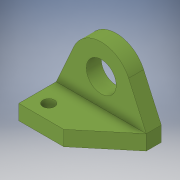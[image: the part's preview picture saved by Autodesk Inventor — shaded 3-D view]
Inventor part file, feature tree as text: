
AUTODESK INVENTOR PART (.ipt)
format: ipt  version: 2018 (Build 220112000, 112)  size: 145,920 bytes
history: native  units: in
note: dims shown in document units (in); Inventor stores cm internally (conversion verified against a paired STEP export)
features: extrude x4, sketch x4, projected_geometry x3, other x3, reference x1
ambient origin geometry x8: Origin, YZ Plane, XZ Plane, XY Plane, X Axis, Y Axis, Z Axis, Center Point
bodies: Solid1 (feature_tree)
feature tree (15):
  extrude  "Extrusion1"  Depth=0.195in
  extrude  "Extrusion2"  Depth=0.25in
  extrude  "Extrusion3"  Depth=0.25in
  extrude  "Extrusion4"  Depth=0.25in TaperAngle=0.0deg
  sketch  "Sketch1"  dims[d0=0.195in d1=0.195in]
  sketch  "Sketch2"  dims[d2=1.0in d3=0.25in]
  projected_geometry  "Projected Loop1"
  reference  "Reference1"
  sketch  "Sketch3"  dims[d4=0.125in d5=0.25in]
  projected_geometry  "Projected Loop2"
  sketch  "Sketch4"  dims[d6=0.75in d7=0.25in d8=0.0in d9=0.25in d10=0.5in d11=0.25in d12=0.0in d13=0.125in d14=0.0in d15=1.0in d16=0.0in]
  projected_geometry  "Projected Loop3"
  parser-record x1  (decoder bookkeeping rows leaked as tree rows — omitted from the tree; the rows remain in map.json)
  other  "Assembly2.iam"
  other  "0_375_Hex_ID_x_1_125_OD_x_0_313_WD_Flanged_Bearing_217-2735:2"
note: 1 file-system path scrubbed to <path> (originals preserved in map.json)
